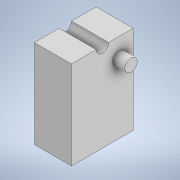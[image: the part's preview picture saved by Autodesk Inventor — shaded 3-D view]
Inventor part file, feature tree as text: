
AUTODESK INVENTOR PART (.ipt)
format: ipt  version: 2021 (Build 250183000, 183)  size: 112,128 bytes
history: native  units: mm
features: extrude x3, sketch x3
ambient origin geometry x8: Origin, YZ Plane, XZ Plane, XY Plane, X Axis, Y Axis, Z Axis, Center Point
bodies: Solid1 (feature_tree)
feature tree (6):
  extrude  "Extrusion1"  Depth=15.0mm
  extrude  "Extrusion2"  Depth=7.5mm
  extrude  "Extrusion3"  Depth=3.0mm
  sketch  "Sketch1"  dims[d0=21.477mm d1=15.0mm]
  sketch  "Sketch2"  dims[d2=10.7385mm d3=7.5mm]
  sketch  "Sketch3"  dims[d4=9.0mm d5=0.0mm d8=3.0mm d10=0.0mm d11=0.0mm d12=3.0mm d13=3.983mm d14=4.478mm d15=3.0mm d16=0.0mm]
